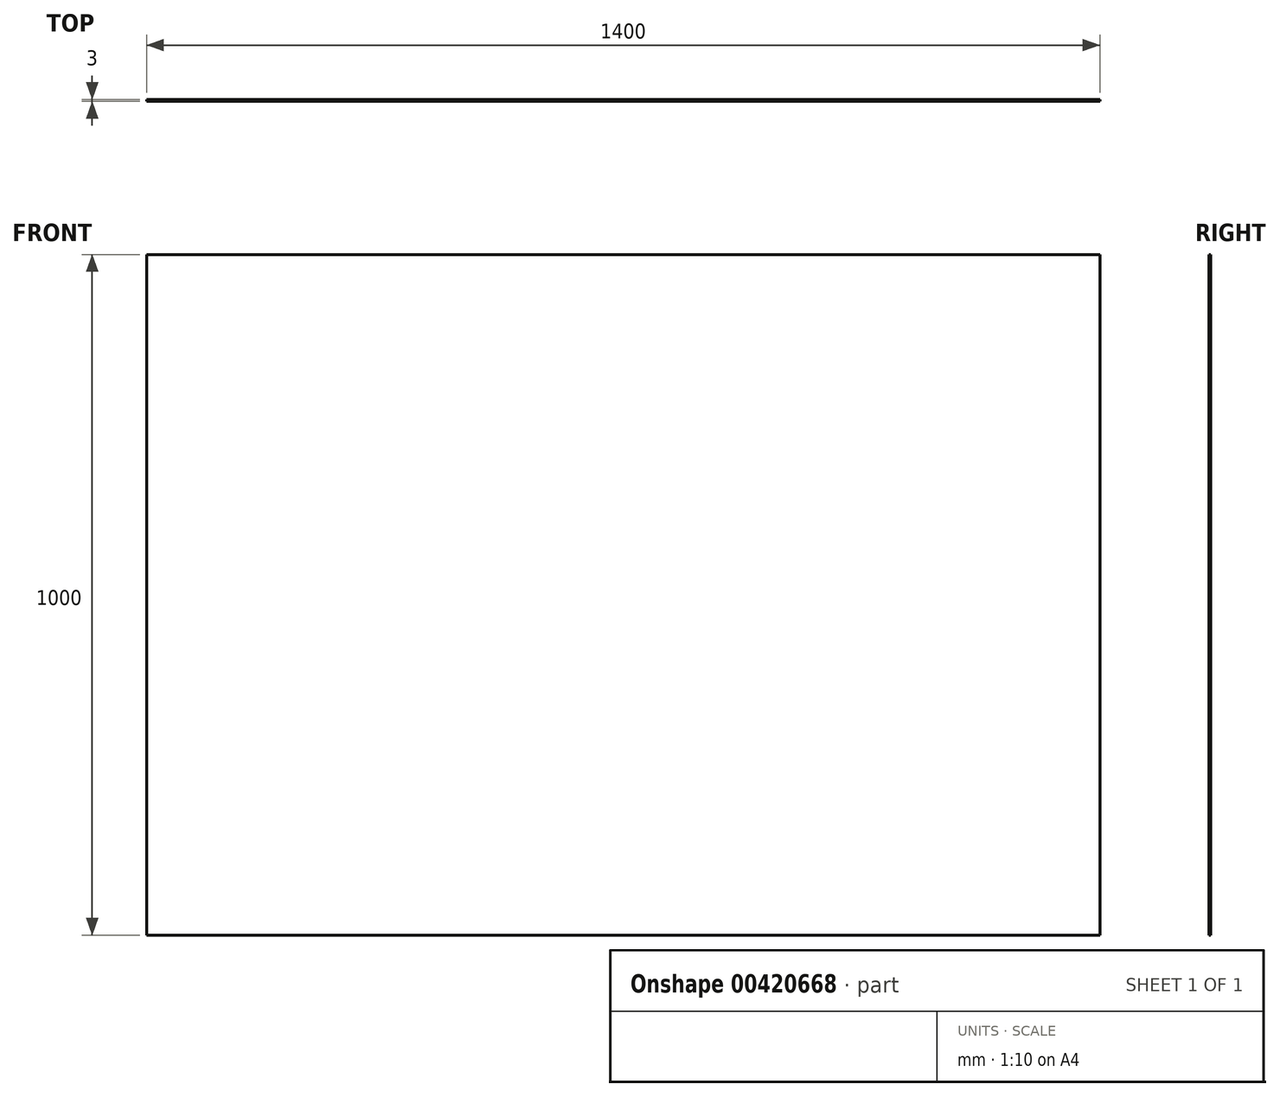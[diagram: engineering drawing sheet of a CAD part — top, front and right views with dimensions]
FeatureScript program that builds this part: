
annotation { "Feature Type Name" : "Feature", "Feature Type Description" : "" }
export const myFeature = defineFeature(function(context is Context, id is Id, definition is map)
    precondition{}
    {
        {
            var Q0;
            Q0=qCreatedBy(makeId("Front.planeOp"),FACE);
            var sketch = newSketch(context, id + "F0", { "sketchPlane" : qUnion([Q0])});
            skLineSegment(sketch, "E0.bottom", {"start": v(700, -500) * mm, "end": v(-700, -500) * mm});
            skLineSegment(sketch, "E0.top", {"start": v(700, 500) * mm, "end": v(-700, 500) * mm});
            skLineSegment(sketch, "E0.left", {"start": v(700, -500) * mm, "end": v(700, 500) * mm});
            skLineSegment(sketch, "E0.right", {"start": v(-700, -500) * mm, "end": v(-700, 500) * mm});
            skPoint(sketch, "E0.middle", {"position": v(0, 0) * mm});
            skSolve(sketch);
        }
        {
            var Q0;
            Q0=qSketchRegion(id+"F0",true);
            extrude(context, id + "F1", {"entities" : qUnion([Q0]), "depth" : 3 * mm});
        }
    });
